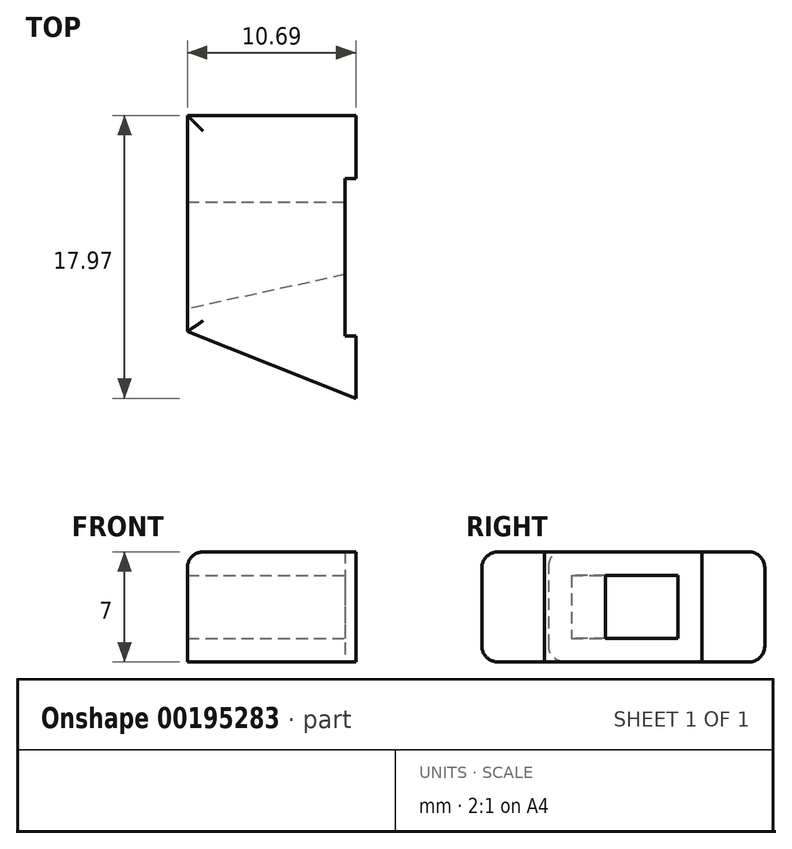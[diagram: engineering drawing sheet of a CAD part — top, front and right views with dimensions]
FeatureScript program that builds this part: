
annotation { "Feature Type Name" : "Feature", "Feature Type Description" : "" }
export const myFeature = defineFeature(function(context is Context, id is Id, definition is map)
    precondition{}
    {
        {
            var Q0;
            Q0=qCreatedBy(makeId("Top.planeOp"),FACE);
            var sketch = newSketch(context, id + "F0", { "sketchPlane" : qUnion([Q0])});
            skLineSegment(sketch, "E0.bottom", {"start": v(54.29, -9) * mm, "end": v(-115.71, -9) * mm});
            skLineSegment(sketch, "E0.top", {"start": v(54.29, 9) * mm, "end": v(-115.71, 9) * mm});
            skLineSegment(sketch, "E0.left", {"start": v(54.29, -9) * mm, "end": v(54.29, 9) * mm});
            skLineSegment(sketch, "E0.right", {"start": v(-115.71, -9) * mm, "end": v(-115.71, 9) * mm});
            skLineSegment(sketch, "E1.bottom", {"start": v(-105.71, 5) * mm, "end": v(50.29, 5) * mm});
            skLineSegment(sketch, "E1.top", {"start": v(-105.71, -5) * mm, "end": v(50.29, -5) * mm});
            skLineSegment(sketch, "E1.left", {"start": v(-105.71, 5) * mm, "end": v(-105.71, -5) * mm});
            skLineSegment(sketch, "E1.right", {"start": v(50.29, 5) * mm, "end": v(50.29, -5) * mm});
            skText(sketch, "E2", { "text": " MAX MAX MAX MAX ", "fontName": "OpenSans-Bold.ttf"});
            const initialGuessF0  = {"E2": [-0.09782, -0.005, 1, 0, 0.01]};
            skSetInitialGuess(sketch, initialGuessF0);
            skSolve(sketch);
        }
        {
            var Q0;
            Q0=makeQuery(id+"F0.imprint","IMPRINT",FACE,{"disambiguationData":[TD([[makeQuery(id+"F0.imprint","IMPRINT",EDGE,{"derivedFrom":sQuery(id+"F0.wireOp",EDGE,"E0.bottom")}),-1.0]])]});
            var Q1;
            Q1=makeQuery(id+"F0.imprint","IMPRINT",FACE,{"disambiguationData":[TD([[makeQuery(id+"F0.imprint","IMPRINT",EDGE,{"derivedFrom":sQuery(id+"F0.wireOp",EDGE,"E2.sketch_text.stroke-0")}),-1.0]])]});
            var Q2;
            Q2=makeQuery(id+"F0.imprint","IMPRINT",FACE,{"disambiguationData":[TD([[makeQuery(id+"F0.imprint","IMPRINT",EDGE,{"derivedFrom":sQuery(id+"F0.wireOp",EDGE,"E2.sketch_text.stroke-19")}),-1.0]])]});
            var Q3;
            Q3=makeQuery(id+"F0.imprint","IMPRINT",FACE,{"disambiguationData":[TD([[makeQuery(id+"F0.imprint","IMPRINT",EDGE,{"derivedFrom":sQuery(id+"F0.wireOp",EDGE,"E2.sketch_text.stroke-31")}),-1.0]])]});
            var Q4;
            Q4=makeQuery(id+"F0.imprint","IMPRINT",FACE,{"disambiguationData":[TD([[makeQuery(id+"F0.imprint","IMPRINT",EDGE,{"derivedFrom":sQuery(id+"F0.wireOp",EDGE,"E2.sketch_text.stroke-43")}),-1.0]])]});
            var Q5;
            Q5=makeQuery(id+"F0.imprint","IMPRINT",FACE,{"disambiguationData":[TD([[makeQuery(id+"F0.imprint","IMPRINT",EDGE,{"derivedFrom":sQuery(id+"F0.wireOp",EDGE,"E2.sketch_text.stroke-62")}),-1.0]])]});
            var Q6;
            Q6=makeQuery(id+"F0.imprint","IMPRINT",FACE,{"disambiguationData":[TD([[makeQuery(id+"F0.imprint","IMPRINT",EDGE,{"derivedFrom":sQuery(id+"F0.wireOp",EDGE,"E2.sketch_text.stroke-74")}),-1.0]])]});
            var Q7;
            Q7=makeQuery(id+"F0.imprint","IMPRINT",FACE,{"disambiguationData":[TD([[makeQuery(id+"F0.imprint","IMPRINT",EDGE,{"derivedFrom":sQuery(id+"F0.wireOp",EDGE,"E2.sketch_text.stroke-86")}),-1.0]])]});
            var Q8;
            Q8=makeQuery(id+"F0.imprint","IMPRINT",FACE,{"disambiguationData":[TD([[makeQuery(id+"F0.imprint","IMPRINT",EDGE,{"derivedFrom":sQuery(id+"F0.wireOp",EDGE,"E2.sketch_text.stroke-105")}),-1.0]])]});
            var Q9;
            Q9=makeQuery(id+"F0.imprint","IMPRINT",FACE,{"disambiguationData":[TD([[makeQuery(id+"F0.imprint","IMPRINT",EDGE,{"derivedFrom":sQuery(id+"F0.wireOp",EDGE,"E2.sketch_text.stroke-117")}),-1.0]])]});
            var Q10;
            Q10=makeQuery(id+"F0.imprint","IMPRINT",FACE,{"disambiguationData":[TD([[makeQuery(id+"F0.imprint","IMPRINT",EDGE,{"derivedFrom":sQuery(id+"F0.wireOp",EDGE,"E2.sketch_text.stroke-129")}),-1.0]])]});
            var Q11;
            Q11=makeQuery(id+"F0.imprint","IMPRINT",FACE,{"disambiguationData":[TD([[makeQuery(id+"F0.imprint","IMPRINT",EDGE,{"derivedFrom":sQuery(id+"F0.wireOp",EDGE,"E2.sketch_text.stroke-148")}),-1.0]])]});
            var Q12;
            Q12=makeQuery(id+"F0.imprint","IMPRINT",FACE,{"disambiguationData":[TD([[makeQuery(id+"F0.imprint","IMPRINT",EDGE,{"derivedFrom":sQuery(id+"F0.wireOp",EDGE,"E2.sketch_text.stroke-160")}),-1.0]])]});
            extrude(context, id + "F1", {"entities" : qUnion([Q0, Q1, Q2, Q3, Q4, Q5, Q6, Q7, Q8, Q9, Q10, Q11, Q12]), "endBound" : BoundingType.SYMMETRIC, "depth" : 7 * mm});
        }
        {
            var Q0;
            Q0=qCreatedBy(makeId("Top.planeOp"),FACE);
            var sketch = newSketch(context, id + "F2", { "sketchPlane" : qUnion([Q0])});
            skLineSegment(sketch, "E3", {"start": v(-116.71, 3.5) * mm, "end": v(-105.21, 3.5) * mm});
            skLineSegment(sketch, "E4", {"start": v(-105.21, -1) * mm, "end": v(-116.71, -3.5) * mm});
            skLineSegment(sketch, "E5", {"start": v(-105.21, 3.5) * mm, "end": v(-105.21, -1) * mm});
            skLineSegment(sketch, "E6", {"start": v(-116.71, 3.5) * mm, "end": v(-116.71, -3.5) * mm});
            skSolve(sketch);
        }
        {
            var Q0;
            Q0=qSketchRegion(id+"F2",true);
            extrude(context, id + "F3", {"entities" : qUnion([Q0]), "operationType" : NewBodyOperationType.REMOVE, "endBound" : BoundingType.SYMMETRIC, "oppositeDirection" : true, "depth" : 4 * mm});
        }
        {
            var Q0;
            Q0=qCreatedBy(makeId("Top.planeOp"),FACE);
            var sketch = newSketch(context, id + "F4", { "sketchPlane" : qUnion([Q0])});
            skLineSegment(sketch, "E7", {"start": v(-104.42, -9.2) * mm, "end": v(-117.77, -3.9) * mm});
            skLineSegment(sketch, "E8", {"start": v(-117.77, -3.9) * mm, "end": v(-117.77, -10.56) * mm});
            skLineSegment(sketch, "E9", {"start": v(-117.77, -10.56) * mm, "end": v(-104.42, -9.2) * mm});
            skSolve(sketch);
        }
        {
            var Q0;
            Q0=qSketchRegion(id+"F4",true);
            extrude(context, id + "F5", {"entities" : qUnion([Q0]), "operationType" : NewBodyOperationType.REMOVE, "endBound" : BoundingType.SYMMETRIC, "depth" : 15 * mm});
        }
        {
            var Q0;
            Q0=makeQuery(id+"F1.opExtrude","CAP_EDGE",EDGE,{"disambiguationData":[OSD([sQuery(id+"F0.wireOp",EDGE,"E0.left")])],"isStart":true});
            var Q1;
            Q1=makeQuery(id+"F1.opExtrude","CAP_EDGE",EDGE,{"disambiguationData":[OSD([sQuery(id+"F0.wireOp",EDGE,"E0.top")])],"isStart":true});
            var Q2;
            Q2=makeQuery(id+"F1.opExtrude","CAP_EDGE",EDGE,{"disambiguationData":[OSD([sQuery(id+"F0.wireOp",EDGE,"E0.bottom")])],"isStart":true});
            var Q3;
            Q3=makeQuery(id+"F1.opExtrude","CAP_EDGE",EDGE,{"disambiguationData":[OSD([sQuery(id+"F0.wireOp",EDGE,"E0.left")])],"isStart":false});
            var Q4;
            Q4=makeQuery(id+"F1.opExtrude","SWEPT_EDGE",EDGE,{"disambiguationData":[OSD([sQuery(id+"F0.wireOp",EDGE,"E0.top"),sQuery(id+"F0.wireOp",EDGE,"E0.left")])]});
            var Q5;
            Q5=makeQuery(id+"F1.opExtrude","SWEPT_EDGE",EDGE,{"disambiguationData":[OSD([sQuery(id+"F0.wireOp",EDGE,"E0.bottom"),sQuery(id+"F0.wireOp",EDGE,"E0.left")])]});
            var Q6;
            Q6=makeQuery(id+"F5.boolean.opBoolean","INTERSECT",EDGE,{"derivedFrom":[makeQuery(id+"F1.opExtrude","CAP_FACE",FACE,{"disambiguationData":[OSD([sQuery(id+"F0.wireOp",EDGE,"E0.bottom"),sQuery(id+"F0.wireOp",EDGE,"E0.top"),sQuery(id+"F0.wireOp",EDGE,"E0.left"),sQuery(id+"F0.wireOp",EDGE,"E0.right"),sQuery(id+"F0.wireOp",EDGE,"E1.bottom"),sQuery(id+"F0.wireOp",EDGE,"E1.top"),sQuery(id+"F0.wireOp",EDGE,"E1.left"),sQuery(id+"F0.wireOp",EDGE,"E1.right"),sQuery(id+"F0.wireOp",EDGE,"E2.sketch_text.stroke-0"),sQuery(id+"F0.wireOp",EDGE,"E2.sketch_text.stroke-1"),sQuery(id+"F0.wireOp",EDGE,"E2.sketch_text.stroke-2"),sQuery(id+"F0.wireOp",EDGE,"E2.sketch_text.stroke-3"),sQuery(id+"F0.wireOp",EDGE,"E2.sketch_text.stroke-5"),sQuery(id+"F0.wireOp",EDGE,"E2.sketch_text.stroke-6"),sQuery(id+"F0.wireOp",EDGE,"E2.sketch_text.stroke-7"),sQuery(id+"F0.wireOp",EDGE,"E2.sketch_text.stroke-8"),sQuery(id+"F0.wireOp",EDGE,"E2.sketch_text.stroke-9"),sQuery(id+"F0.wireOp",EDGE,"E2.sketch_text.stroke-10"),sQuery(id+"F0.wireOp",EDGE,"E2.sketch_text.stroke-11"),sQuery(id+"F0.wireOp",EDGE,"E2.sketch_text.stroke-13"),sQuery(id+"F0.wireOp",EDGE,"E2.sketch_text.stroke-14"),sQuery(id+"F0.wireOp",EDGE,"E2.sketch_text.stroke-15"),sQuery(id+"F0.wireOp",EDGE,"E2.sketch_text.stroke-16"),sQuery(id+"F0.wireOp",EDGE,"E2.sketch_text.stroke-17"),sQuery(id+"F0.wireOp",EDGE,"E2.sketch_text.stroke-19"),sQuery(id+"F0.wireOp",EDGE,"E2.sketch_text.stroke-20"),sQuery(id+"F0.wireOp",EDGE,"E2.sketch_text.stroke-21"),sQuery(id+"F0.wireOp",EDGE,"E2.sketch_text.stroke-23"),sQuery(id+"F0.wireOp",EDGE,"E2.sketch_text.stroke-24"),sQuery(id+"F0.wireOp",EDGE,"E2.sketch_text.stroke-25"),sQuery(id+"F0.wireOp",EDGE,"E2.sketch_text.stroke-27"),sQuery(id+"F0.wireOp",EDGE,"E2.sketch_text.stroke-28"),sQuery(id+"F0.wireOp",EDGE,"E2.sketch_text.stroke-29"),sQuery(id+"F0.wireOp",EDGE,"E2.sketch_text.stroke-30"),sQuery(id+"F0.wireOp",EDGE,"E2.sketch_text.stroke-32"),sQuery(id+"F0.wireOp",EDGE,"E2.sketch_text.stroke-33"),sQuery(id+"F0.wireOp",EDGE,"E2.sketch_text.stroke-35"),sQuery(id+"F0.wireOp",EDGE,"E2.sketch_text.stroke-36"),sQuery(id+"F0.wireOp",EDGE,"E2.sketch_text.stroke-37"),sQuery(id+"F0.wireOp",EDGE,"E2.sketch_text.stroke-38"),sQuery(id+"F0.wireOp",EDGE,"E2.sketch_text.stroke-39"),sQuery(id+"F0.wireOp",EDGE,"E2.sketch_text.stroke-40"),sQuery(id+"F0.wireOp",EDGE,"E2.sketch_text.stroke-41"),sQuery(id+"F0.wireOp",EDGE,"E2.sketch_text.stroke-42"),sQuery(id+"F0.wireOp",EDGE,"E2.sketch_text.stroke-43"),sQuery(id+"F0.wireOp",EDGE,"E2.sketch_text.stroke-44"),sQuery(id+"F0.wireOp",EDGE,"E2.sketch_text.stroke-45"),sQuery(id+"F0.wireOp",EDGE,"E2.sketch_text.stroke-46"),sQuery(id+"F0.wireOp",EDGE,"E2.sketch_text.stroke-48"),sQuery(id+"F0.wireOp",EDGE,"E2.sketch_text.stroke-49"),sQuery(id+"F0.wireOp",EDGE,"E2.sketch_text.stroke-50"),sQuery(id+"F0.wireOp",EDGE,"E2.sketch_text.stroke-51"),sQuery(id+"F0.wireOp",EDGE,"E2.sketch_text.stroke-52"),sQuery(id+"F0.wireOp",EDGE,"E2.sketch_text.stroke-53"),sQuery(id+"F0.wireOp",EDGE,"E2.sketch_text.stroke-54"),sQuery(id+"F0.wireOp",EDGE,"E2.sketch_text.stroke-56"),sQuery(id+"F0.wireOp",EDGE,"E2.sketch_text.stroke-57"),sQuery(id+"F0.wireOp",EDGE,"E2.sketch_text.stroke-58"),sQuery(id+"F0.wireOp",EDGE,"E2.sketch_text.stroke-59"),sQuery(id+"F0.wireOp",EDGE,"E2.sketch_text.stroke-60"),sQuery(id+"F0.wireOp",EDGE,"E2.sketch_text.stroke-62"),sQuery(id+"F0.wireOp",EDGE,"E2.sketch_text.stroke-63"),sQuery(id+"F0.wireOp",EDGE,"E2.sketch_text.stroke-64"),sQuery(id+"F0.wireOp",EDGE,"E2.sketch_text.stroke-66"),sQuery(id+"F0.wireOp",EDGE,"E2.sketch_text.stroke-67"),sQuery(id+"F0.wireOp",EDGE,"E2.sketch_text.stroke-68"),sQuery(id+"F0.wireOp",EDGE,"E2.sketch_text.stroke-70"),sQuery(id+"F0.wireOp",EDGE,"E2.sketch_text.stroke-71"),sQuery(id+"F0.wireOp",EDGE,"E2.sketch_text.stroke-72"),sQuery(id+"F0.wireOp",EDGE,"E2.sketch_text.stroke-73"),sQuery(id+"F0.wireOp",EDGE,"E2.sketch_text.stroke-75"),sQuery(id+"F0.wireOp",EDGE,"E2.sketch_text.stroke-76"),sQuery(id+"F0.wireOp",EDGE,"E2.sketch_text.stroke-78"),sQuery(id+"F0.wireOp",EDGE,"E2.sketch_text.stroke-79"),sQuery(id+"F0.wireOp",EDGE,"E2.sketch_text.stroke-80"),sQuery(id+"F0.wireOp",EDGE,"E2.sketch_text.stroke-81"),sQuery(id+"F0.wireOp",EDGE,"E2.sketch_text.stroke-82"),sQuery(id+"F0.wireOp",EDGE,"E2.sketch_text.stroke-83"),sQuery(id+"F0.wireOp",EDGE,"E2.sketch_text.stroke-84"),sQuery(id+"F0.wireOp",EDGE,"E2.sketch_text.stroke-85"),sQuery(id+"F0.wireOp",EDGE,"E2.sketch_text.stroke-86"),sQuery(id+"F0.wireOp",EDGE,"E2.sketch_text.stroke-87"),sQuery(id+"F0.wireOp",EDGE,"E2.sketch_text.stroke-88"),sQuery(id+"F0.wireOp",EDGE,"E2.sketch_text.stroke-89"),sQuery(id+"F0.wireOp",EDGE,"E2.sketch_text.stroke-91"),sQuery(id+"F0.wireOp",EDGE,"E2.sketch_text.stroke-92"),sQuery(id+"F0.wireOp",EDGE,"E2.sketch_text.stroke-93"),sQuery(id+"F0.wireOp",EDGE,"E2.sketch_text.stroke-94"),sQuery(id+"F0.wireOp",EDGE,"E2.sketch_text.stroke-95"),sQuery(id+"F0.wireOp",EDGE,"E2.sketch_text.stroke-96"),sQuery(id+"F0.wireOp",EDGE,"E2.sketch_text.stroke-97"),sQuery(id+"F0.wireOp",EDGE,"E2.sketch_text.stroke-99"),sQuery(id+"F0.wireOp",EDGE,"E2.sketch_text.stroke-100"),sQuery(id+"F0.wireOp",EDGE,"E2.sketch_text.stroke-101"),sQuery(id+"F0.wireOp",EDGE,"E2.sketch_text.stroke-102"),sQuery(id+"F0.wireOp",EDGE,"E2.sketch_text.stroke-103"),sQuery(id+"F0.wireOp",EDGE,"E2.sketch_text.stroke-105"),sQuery(id+"F0.wireOp",EDGE,"E2.sketch_text.stroke-106"),sQuery(id+"F0.wireOp",EDGE,"E2.sketch_text.stroke-107"),sQuery(id+"F0.wireOp",EDGE,"E2.sketch_text.stroke-109"),sQuery(id+"F0.wireOp",EDGE,"E2.sketch_text.stroke-110"),sQuery(id+"F0.wireOp",EDGE,"E2.sketch_text.stroke-111"),sQuery(id+"F0.wireOp",EDGE,"E2.sketch_text.stroke-113"),sQuery(id+"F0.wireOp",EDGE,"E2.sketch_text.stroke-114"),sQuery(id+"F0.wireOp",EDGE,"E2.sketch_text.stroke-115"),sQuery(id+"F0.wireOp",EDGE,"E2.sketch_text.stroke-116"),sQuery(id+"F0.wireOp",EDGE,"E2.sketch_text.stroke-118"),sQuery(id+"F0.wireOp",EDGE,"E2.sketch_text.stroke-119"),sQuery(id+"F0.wireOp",EDGE,"E2.sketch_text.stroke-121"),sQuery(id+"F0.wireOp",EDGE,"E2.sketch_text.stroke-122"),sQuery(id+"F0.wireOp",EDGE,"E2.sketch_text.stroke-123"),sQuery(id+"F0.wireOp",EDGE,"E2.sketch_text.stroke-124"),sQuery(id+"F0.wireOp",EDGE,"E2.sketch_text.stroke-125"),sQuery(id+"F0.wireOp",EDGE,"E2.sketch_text.stroke-126"),sQuery(id+"F0.wireOp",EDGE,"E2.sketch_text.stroke-127"),sQuery(id+"F0.wireOp",EDGE,"E2.sketch_text.stroke-128"),sQuery(id+"F0.wireOp",EDGE,"E2.sketch_text.stroke-129"),sQuery(id+"F0.wireOp",EDGE,"E2.sketch_text.stroke-130"),sQuery(id+"F0.wireOp",EDGE,"E2.sketch_text.stroke-131"),sQuery(id+"F0.wireOp",EDGE,"E2.sketch_text.stroke-132"),sQuery(id+"F0.wireOp",EDGE,"E2.sketch_text.stroke-134"),sQuery(id+"F0.wireOp",EDGE,"E2.sketch_text.stroke-135"),sQuery(id+"F0.wireOp",EDGE,"E2.sketch_text.stroke-136"),sQuery(id+"F0.wireOp",EDGE,"E2.sketch_text.stroke-137"),sQuery(id+"F0.wireOp",EDGE,"E2.sketch_text.stroke-138"),sQuery(id+"F0.wireOp",EDGE,"E2.sketch_text.stroke-139"),sQuery(id+"F0.wireOp",EDGE,"E2.sketch_text.stroke-140"),sQuery(id+"F0.wireOp",EDGE,"E2.sketch_text.stroke-142"),sQuery(id+"F0.wireOp",EDGE,"E2.sketch_text.stroke-143"),sQuery(id+"F0.wireOp",EDGE,"E2.sketch_text.stroke-144"),sQuery(id+"F0.wireOp",EDGE,"E2.sketch_text.stroke-145"),sQuery(id+"F0.wireOp",EDGE,"E2.sketch_text.stroke-146"),sQuery(id+"F0.wireOp",EDGE,"E2.sketch_text.stroke-148"),sQuery(id+"F0.wireOp",EDGE,"E2.sketch_text.stroke-149"),sQuery(id+"F0.wireOp",EDGE,"E2.sketch_text.stroke-150"),sQuery(id+"F0.wireOp",EDGE,"E2.sketch_text.stroke-152"),sQuery(id+"F0.wireOp",EDGE,"E2.sketch_text.stroke-153"),sQuery(id+"F0.wireOp",EDGE,"E2.sketch_text.stroke-154"),sQuery(id+"F0.wireOp",EDGE,"E2.sketch_text.stroke-156"),sQuery(id+"F0.wireOp",EDGE,"E2.sketch_text.stroke-157"),sQuery(id+"F0.wireOp",EDGE,"E2.sketch_text.stroke-158"),sQuery(id+"F0.wireOp",EDGE,"E2.sketch_text.stroke-159"),sQuery(id+"F0.wireOp",EDGE,"E2.sketch_text.stroke-161"),sQuery(id+"F0.wireOp",EDGE,"E2.sketch_text.stroke-162"),sQuery(id+"F0.wireOp",EDGE,"E2.sketch_text.stroke-164"),sQuery(id+"F0.wireOp",EDGE,"E2.sketch_text.stroke-165"),sQuery(id+"F0.wireOp",EDGE,"E2.sketch_text.stroke-166"),sQuery(id+"F0.wireOp",EDGE,"E2.sketch_text.stroke-167"),sQuery(id+"F0.wireOp",EDGE,"E2.sketch_text.stroke-168"),sQuery(id+"F0.wireOp",EDGE,"E2.sketch_text.stroke-169"),sQuery(id+"F0.wireOp",EDGE,"E2.sketch_text.stroke-170"),sQuery(id+"F0.wireOp",EDGE,"E2.sketch_text.stroke-171")])],"isStart":true}),makeQuery(id+"F5.opExtrude","SWEPT_FACE",FACE,{"disambiguationData":[OSD([sQuery(id+"F4.wireOp",EDGE,"E7")])]})]});
            var Q7;
            Q7=makeQuery(id+"F1.opExtrude","CAP_EDGE",EDGE,{"disambiguationData":[OSD([sQuery(id+"F0.wireOp",EDGE,"E0.bottom")])],"isStart":false});
            var Q8;
            Q8=makeQuery(id+"F1.opExtrude","CAP_EDGE",EDGE,{"disambiguationData":[OSD([sQuery(id+"F0.wireOp",EDGE,"E0.top")])],"isStart":false});
            var Q9;
            Q9=makeQuery(id+"F1.opExtrude","CAP_EDGE",EDGE,{"disambiguationData":[OSD([sQuery(id+"F0.wireOp",EDGE,"E0.right")])],"isStart":false});
            var Q10;
            Q10=makeQuery(id+"F5.boolean.opBoolean","INTERSECT",EDGE,{"derivedFrom":[makeQuery(id+"F1.opExtrude","CAP_FACE",FACE,{"disambiguationData":[OSD([sQuery(id+"F0.wireOp",EDGE,"E0.bottom"),sQuery(id+"F0.wireOp",EDGE,"E0.top"),sQuery(id+"F0.wireOp",EDGE,"E0.left"),sQuery(id+"F0.wireOp",EDGE,"E0.right"),sQuery(id+"F0.wireOp",EDGE,"E1.bottom"),sQuery(id+"F0.wireOp",EDGE,"E1.top"),sQuery(id+"F0.wireOp",EDGE,"E1.left"),sQuery(id+"F0.wireOp",EDGE,"E1.right"),sQuery(id+"F0.wireOp",EDGE,"E2.sketch_text.stroke-0"),sQuery(id+"F0.wireOp",EDGE,"E2.sketch_text.stroke-1"),sQuery(id+"F0.wireOp",EDGE,"E2.sketch_text.stroke-2"),sQuery(id+"F0.wireOp",EDGE,"E2.sketch_text.stroke-3"),sQuery(id+"F0.wireOp",EDGE,"E2.sketch_text.stroke-5"),sQuery(id+"F0.wireOp",EDGE,"E2.sketch_text.stroke-6"),sQuery(id+"F0.wireOp",EDGE,"E2.sketch_text.stroke-7"),sQuery(id+"F0.wireOp",EDGE,"E2.sketch_text.stroke-8"),sQuery(id+"F0.wireOp",EDGE,"E2.sketch_text.stroke-9"),sQuery(id+"F0.wireOp",EDGE,"E2.sketch_text.stroke-10"),sQuery(id+"F0.wireOp",EDGE,"E2.sketch_text.stroke-11"),sQuery(id+"F0.wireOp",EDGE,"E2.sketch_text.stroke-13"),sQuery(id+"F0.wireOp",EDGE,"E2.sketch_text.stroke-14"),sQuery(id+"F0.wireOp",EDGE,"E2.sketch_text.stroke-15"),sQuery(id+"F0.wireOp",EDGE,"E2.sketch_text.stroke-16"),sQuery(id+"F0.wireOp",EDGE,"E2.sketch_text.stroke-17"),sQuery(id+"F0.wireOp",EDGE,"E2.sketch_text.stroke-19"),sQuery(id+"F0.wireOp",EDGE,"E2.sketch_text.stroke-20"),sQuery(id+"F0.wireOp",EDGE,"E2.sketch_text.stroke-21"),sQuery(id+"F0.wireOp",EDGE,"E2.sketch_text.stroke-23"),sQuery(id+"F0.wireOp",EDGE,"E2.sketch_text.stroke-24"),sQuery(id+"F0.wireOp",EDGE,"E2.sketch_text.stroke-25"),sQuery(id+"F0.wireOp",EDGE,"E2.sketch_text.stroke-27"),sQuery(id+"F0.wireOp",EDGE,"E2.sketch_text.stroke-28"),sQuery(id+"F0.wireOp",EDGE,"E2.sketch_text.stroke-29"),sQuery(id+"F0.wireOp",EDGE,"E2.sketch_text.stroke-30"),sQuery(id+"F0.wireOp",EDGE,"E2.sketch_text.stroke-32"),sQuery(id+"F0.wireOp",EDGE,"E2.sketch_text.stroke-33"),sQuery(id+"F0.wireOp",EDGE,"E2.sketch_text.stroke-35"),sQuery(id+"F0.wireOp",EDGE,"E2.sketch_text.stroke-36"),sQuery(id+"F0.wireOp",EDGE,"E2.sketch_text.stroke-37"),sQuery(id+"F0.wireOp",EDGE,"E2.sketch_text.stroke-38"),sQuery(id+"F0.wireOp",EDGE,"E2.sketch_text.stroke-39"),sQuery(id+"F0.wireOp",EDGE,"E2.sketch_text.stroke-40"),sQuery(id+"F0.wireOp",EDGE,"E2.sketch_text.stroke-41"),sQuery(id+"F0.wireOp",EDGE,"E2.sketch_text.stroke-42"),sQuery(id+"F0.wireOp",EDGE,"E2.sketch_text.stroke-43"),sQuery(id+"F0.wireOp",EDGE,"E2.sketch_text.stroke-44"),sQuery(id+"F0.wireOp",EDGE,"E2.sketch_text.stroke-45"),sQuery(id+"F0.wireOp",EDGE,"E2.sketch_text.stroke-46"),sQuery(id+"F0.wireOp",EDGE,"E2.sketch_text.stroke-48"),sQuery(id+"F0.wireOp",EDGE,"E2.sketch_text.stroke-49"),sQuery(id+"F0.wireOp",EDGE,"E2.sketch_text.stroke-50"),sQuery(id+"F0.wireOp",EDGE,"E2.sketch_text.stroke-51"),sQuery(id+"F0.wireOp",EDGE,"E2.sketch_text.stroke-52"),sQuery(id+"F0.wireOp",EDGE,"E2.sketch_text.stroke-53"),sQuery(id+"F0.wireOp",EDGE,"E2.sketch_text.stroke-54"),sQuery(id+"F0.wireOp",EDGE,"E2.sketch_text.stroke-56"),sQuery(id+"F0.wireOp",EDGE,"E2.sketch_text.stroke-57"),sQuery(id+"F0.wireOp",EDGE,"E2.sketch_text.stroke-58"),sQuery(id+"F0.wireOp",EDGE,"E2.sketch_text.stroke-59"),sQuery(id+"F0.wireOp",EDGE,"E2.sketch_text.stroke-60"),sQuery(id+"F0.wireOp",EDGE,"E2.sketch_text.stroke-62"),sQuery(id+"F0.wireOp",EDGE,"E2.sketch_text.stroke-63"),sQuery(id+"F0.wireOp",EDGE,"E2.sketch_text.stroke-64"),sQuery(id+"F0.wireOp",EDGE,"E2.sketch_text.stroke-66"),sQuery(id+"F0.wireOp",EDGE,"E2.sketch_text.stroke-67"),sQuery(id+"F0.wireOp",EDGE,"E2.sketch_text.stroke-68"),sQuery(id+"F0.wireOp",EDGE,"E2.sketch_text.stroke-70"),sQuery(id+"F0.wireOp",EDGE,"E2.sketch_text.stroke-71"),sQuery(id+"F0.wireOp",EDGE,"E2.sketch_text.stroke-72"),sQuery(id+"F0.wireOp",EDGE,"E2.sketch_text.stroke-73"),sQuery(id+"F0.wireOp",EDGE,"E2.sketch_text.stroke-75"),sQuery(id+"F0.wireOp",EDGE,"E2.sketch_text.stroke-76"),sQuery(id+"F0.wireOp",EDGE,"E2.sketch_text.stroke-78"),sQuery(id+"F0.wireOp",EDGE,"E2.sketch_text.stroke-79"),sQuery(id+"F0.wireOp",EDGE,"E2.sketch_text.stroke-80"),sQuery(id+"F0.wireOp",EDGE,"E2.sketch_text.stroke-81"),sQuery(id+"F0.wireOp",EDGE,"E2.sketch_text.stroke-82"),sQuery(id+"F0.wireOp",EDGE,"E2.sketch_text.stroke-83"),sQuery(id+"F0.wireOp",EDGE,"E2.sketch_text.stroke-84"),sQuery(id+"F0.wireOp",EDGE,"E2.sketch_text.stroke-85"),sQuery(id+"F0.wireOp",EDGE,"E2.sketch_text.stroke-86"),sQuery(id+"F0.wireOp",EDGE,"E2.sketch_text.stroke-87"),sQuery(id+"F0.wireOp",EDGE,"E2.sketch_text.stroke-88"),sQuery(id+"F0.wireOp",EDGE,"E2.sketch_text.stroke-89"),sQuery(id+"F0.wireOp",EDGE,"E2.sketch_text.stroke-91"),sQuery(id+"F0.wireOp",EDGE,"E2.sketch_text.stroke-92"),sQuery(id+"F0.wireOp",EDGE,"E2.sketch_text.stroke-93"),sQuery(id+"F0.wireOp",EDGE,"E2.sketch_text.stroke-94"),sQuery(id+"F0.wireOp",EDGE,"E2.sketch_text.stroke-95"),sQuery(id+"F0.wireOp",EDGE,"E2.sketch_text.stroke-96"),sQuery(id+"F0.wireOp",EDGE,"E2.sketch_text.stroke-97"),sQuery(id+"F0.wireOp",EDGE,"E2.sketch_text.stroke-99"),sQuery(id+"F0.wireOp",EDGE,"E2.sketch_text.stroke-100"),sQuery(id+"F0.wireOp",EDGE,"E2.sketch_text.stroke-101"),sQuery(id+"F0.wireOp",EDGE,"E2.sketch_text.stroke-102"),sQuery(id+"F0.wireOp",EDGE,"E2.sketch_text.stroke-103"),sQuery(id+"F0.wireOp",EDGE,"E2.sketch_text.stroke-105"),sQuery(id+"F0.wireOp",EDGE,"E2.sketch_text.stroke-106"),sQuery(id+"F0.wireOp",EDGE,"E2.sketch_text.stroke-107"),sQuery(id+"F0.wireOp",EDGE,"E2.sketch_text.stroke-109"),sQuery(id+"F0.wireOp",EDGE,"E2.sketch_text.stroke-110"),sQuery(id+"F0.wireOp",EDGE,"E2.sketch_text.stroke-111"),sQuery(id+"F0.wireOp",EDGE,"E2.sketch_text.stroke-113"),sQuery(id+"F0.wireOp",EDGE,"E2.sketch_text.stroke-114"),sQuery(id+"F0.wireOp",EDGE,"E2.sketch_text.stroke-115"),sQuery(id+"F0.wireOp",EDGE,"E2.sketch_text.stroke-116"),sQuery(id+"F0.wireOp",EDGE,"E2.sketch_text.stroke-118"),sQuery(id+"F0.wireOp",EDGE,"E2.sketch_text.stroke-119"),sQuery(id+"F0.wireOp",EDGE,"E2.sketch_text.stroke-121"),sQuery(id+"F0.wireOp",EDGE,"E2.sketch_text.stroke-122"),sQuery(id+"F0.wireOp",EDGE,"E2.sketch_text.stroke-123"),sQuery(id+"F0.wireOp",EDGE,"E2.sketch_text.stroke-124"),sQuery(id+"F0.wireOp",EDGE,"E2.sketch_text.stroke-125"),sQuery(id+"F0.wireOp",EDGE,"E2.sketch_text.stroke-126"),sQuery(id+"F0.wireOp",EDGE,"E2.sketch_text.stroke-127"),sQuery(id+"F0.wireOp",EDGE,"E2.sketch_text.stroke-128"),sQuery(id+"F0.wireOp",EDGE,"E2.sketch_text.stroke-129"),sQuery(id+"F0.wireOp",EDGE,"E2.sketch_text.stroke-130"),sQuery(id+"F0.wireOp",EDGE,"E2.sketch_text.stroke-131"),sQuery(id+"F0.wireOp",EDGE,"E2.sketch_text.stroke-132"),sQuery(id+"F0.wireOp",EDGE,"E2.sketch_text.stroke-134"),sQuery(id+"F0.wireOp",EDGE,"E2.sketch_text.stroke-135"),sQuery(id+"F0.wireOp",EDGE,"E2.sketch_text.stroke-136"),sQuery(id+"F0.wireOp",EDGE,"E2.sketch_text.stroke-137"),sQuery(id+"F0.wireOp",EDGE,"E2.sketch_text.stroke-138"),sQuery(id+"F0.wireOp",EDGE,"E2.sketch_text.stroke-139"),sQuery(id+"F0.wireOp",EDGE,"E2.sketch_text.stroke-140"),sQuery(id+"F0.wireOp",EDGE,"E2.sketch_text.stroke-142"),sQuery(id+"F0.wireOp",EDGE,"E2.sketch_text.stroke-143"),sQuery(id+"F0.wireOp",EDGE,"E2.sketch_text.stroke-144"),sQuery(id+"F0.wireOp",EDGE,"E2.sketch_text.stroke-145"),sQuery(id+"F0.wireOp",EDGE,"E2.sketch_text.stroke-146"),sQuery(id+"F0.wireOp",EDGE,"E2.sketch_text.stroke-148"),sQuery(id+"F0.wireOp",EDGE,"E2.sketch_text.stroke-149"),sQuery(id+"F0.wireOp",EDGE,"E2.sketch_text.stroke-150"),sQuery(id+"F0.wireOp",EDGE,"E2.sketch_text.stroke-152"),sQuery(id+"F0.wireOp",EDGE,"E2.sketch_text.stroke-153"),sQuery(id+"F0.wireOp",EDGE,"E2.sketch_text.stroke-154"),sQuery(id+"F0.wireOp",EDGE,"E2.sketch_text.stroke-156"),sQuery(id+"F0.wireOp",EDGE,"E2.sketch_text.stroke-157"),sQuery(id+"F0.wireOp",EDGE,"E2.sketch_text.stroke-158"),sQuery(id+"F0.wireOp",EDGE,"E2.sketch_text.stroke-159"),sQuery(id+"F0.wireOp",EDGE,"E2.sketch_text.stroke-161"),sQuery(id+"F0.wireOp",EDGE,"E2.sketch_text.stroke-162"),sQuery(id+"F0.wireOp",EDGE,"E2.sketch_text.stroke-164"),sQuery(id+"F0.wireOp",EDGE,"E2.sketch_text.stroke-165"),sQuery(id+"F0.wireOp",EDGE,"E2.sketch_text.stroke-166"),sQuery(id+"F0.wireOp",EDGE,"E2.sketch_text.stroke-167"),sQuery(id+"F0.wireOp",EDGE,"E2.sketch_text.stroke-168"),sQuery(id+"F0.wireOp",EDGE,"E2.sketch_text.stroke-169"),sQuery(id+"F0.wireOp",EDGE,"E2.sketch_text.stroke-170"),sQuery(id+"F0.wireOp",EDGE,"E2.sketch_text.stroke-171")])],"isStart":false}),makeQuery(id+"F5.opExtrude","SWEPT_FACE",FACE,{"disambiguationData":[OSD([sQuery(id+"F4.wireOp",EDGE,"E7")])]})]});
            fillet(context, id + "F6", {"entities" : qUnion([Q0, Q1, Q2, Q3, Q4, Q5, Q6, Q7, Q8, Q9, Q10]), "radius" : 1 * mm, "tangentPropagation" : true, "allowEdgeOverflow" : false});
        }
        {
            var Q0;
            Q0=qCreatedBy(makeId("Top.planeOp"),FACE);
            var sketch = newSketch(context, id + "F7", { "sketchPlane" : qUnion([Q0])});
            skLineSegment(sketch, "E10.bottom", {"start": v(-105.02, 12.02) * mm, "end": v(55.97, 12.02) * mm});
            skLineSegment(sketch, "E10.top", {"start": v(-105.02, -13.81) * mm, "end": v(55.97, -13.81) * mm});
            skLineSegment(sketch, "E10.left", {"start": v(-105.02, 12.02) * mm, "end": v(-105.02, -13.81) * mm});
            skLineSegment(sketch, "E10.right", {"start": v(55.97, 12.02) * mm, "end": v(55.97, -13.81) * mm});
            skSolve(sketch);
        }
        {
            var Q0;
            Q0 = qSketchRegion(id + "F7", true);
            extrude(context, id + "F8", {"entities" : qUnion([Q0]), "operationType" : NewBodyOperationType.REMOVE, "endBound" : BoundingType.SYMMETRIC, "oppositeDirection" : true, "depth" : 25 * mm});
        }
    });
